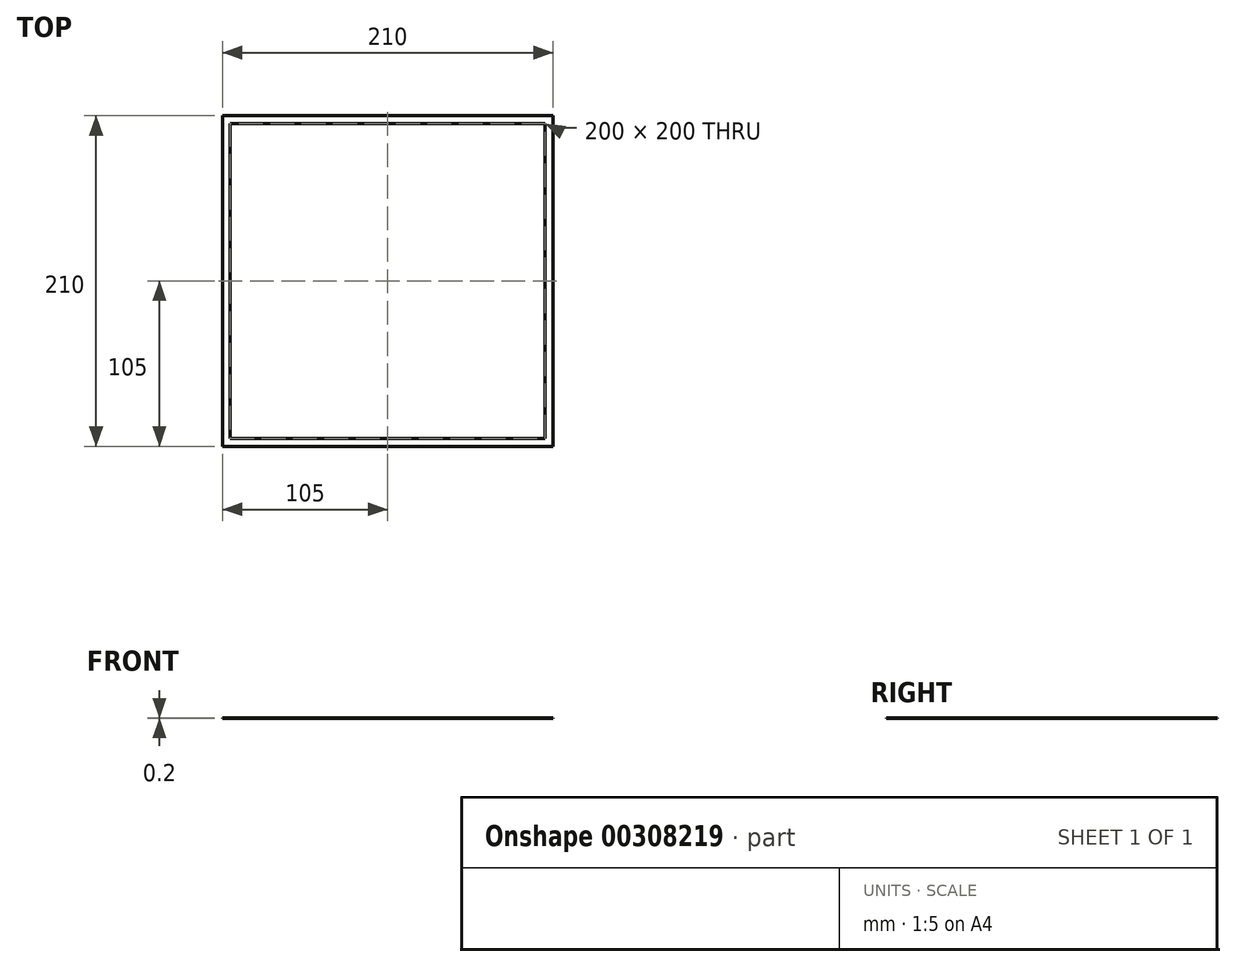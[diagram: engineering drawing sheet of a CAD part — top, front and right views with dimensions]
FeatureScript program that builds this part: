
annotation { "Feature Type Name" : "Feature", "Feature Type Description" : "" }
export const myFeature = defineFeature(function(context is Context, id is Id, definition is map)
    precondition{}
    {
        {
            var Q0;
            Q0=qCreatedBy(makeId("Top.planeOp"),FACE);
            var sketch = newSketch(context, id + "F0", { "sketchPlane" : qUnion([Q0])});
            skLineSegment(sketch, "E0.bottom", {"start": v(-100, 100) * mm, "end": v(100, 100) * mm});
            skLineSegment(sketch, "E0.top", {"start": v(-100, -100) * mm, "end": v(100, -100) * mm});
            skLineSegment(sketch, "E0.left", {"start": v(-100, 100) * mm, "end": v(-100, -100) * mm});
            skLineSegment(sketch, "E0.right", {"start": v(100, 100) * mm, "end": v(100, -100) * mm});
            skPoint(sketch, "E0.middle", {"position": v(0, 0) * mm});
            skLineSegment(sketch, "E1.bottom", {"start": v(-105, 105) * mm, "end": v(105, 105) * mm});
            skLineSegment(sketch, "E1.top", {"start": v(-105, -105) * mm, "end": v(105, -105) * mm});
            skLineSegment(sketch, "E1.left", {"start": v(-105, 105) * mm, "end": v(-105, -105) * mm});
            skLineSegment(sketch, "E1.right", {"start": v(105, 105) * mm, "end": v(105, -105) * mm});
            skSolve(sketch);
        }
        {
            var Q0;
            Q0 = qSketchRegion(id + "F0", true);
            extrude(context, id + "F1", {"entities" : qUnion([Q0]), "depth" : .2 * mm, "offsetDistance" : 25 * mm});
        }
    });
